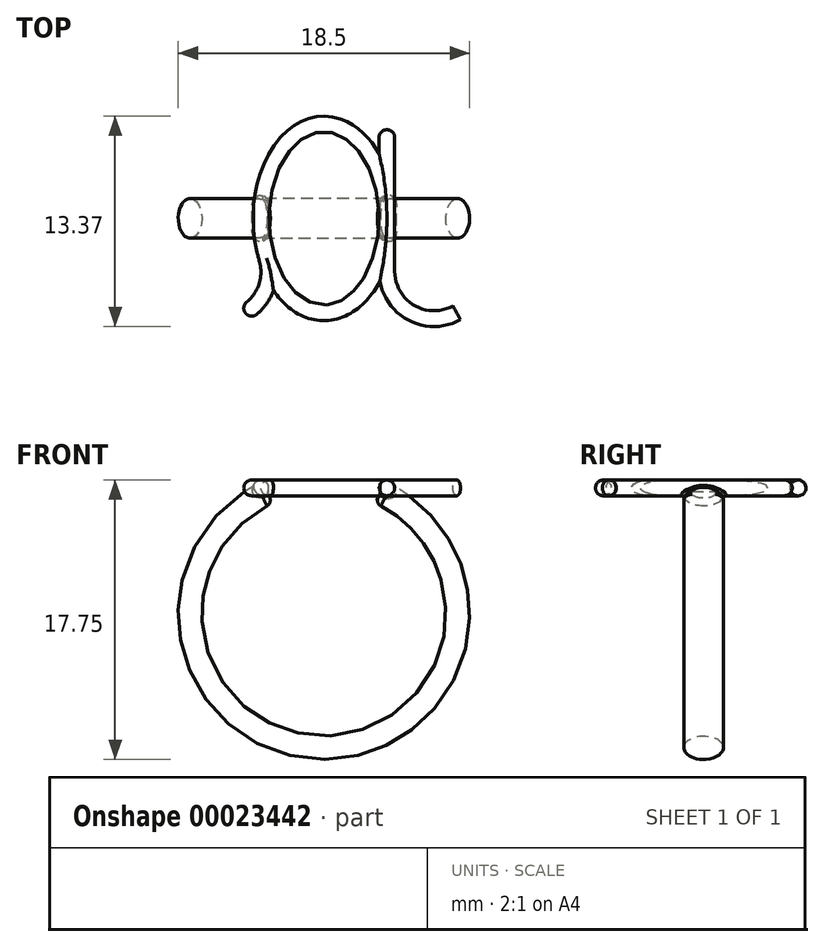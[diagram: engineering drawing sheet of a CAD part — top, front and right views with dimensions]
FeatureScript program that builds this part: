
annotation { "Feature Type Name" : "Feature", "Feature Type Description" : "" }
export const myFeature = defineFeature(function(context is Context, id is Id, definition is map)
    precondition{}
    {
        {
            var Q0;
            Q0=qCreatedBy(makeId("Right.planeOp"),FACE);
            var sketch = newSketch(context, id + "F0", { "sketchPlane" : qUnion([Q0])});
            skEllipse(sketch, "E0", {"center": v(0, -8.5) * mm, "majorRadius": 1.25 * mm, "minorRadius": 0.75 * mm, "majorAxis": v(1, 0)});
            skLineSegment(sketch, "E1", {"start": v(-8.37, 0) * mm, "end": v(10.93, 0) * mm, "construction": true});
            skSolve(sketch);
        }
        {
            var Q0;
            Q0=makeQuery(id+"F0.imprint","IMPRINT",FACE,{"disambiguationData":[TD([[makeQuery(id+"F0.imprint","IMPRINT",EDGE,{"derivedFrom":sQuery(id+"F0.wireOp",EDGE,"E0")}),1.0]])]});
            var Q1;
            Q1=sQuery(id+"F0.wireOp",EDGE,"E1");
            revolve(context, id + "F1", {"entities" : qUnion([Q0]), "axis" : qUnion([Q1]), "revolveType" : RevolveType.TWO_DIRECTIONS, "angle" : 155 * degree, "angleBack" : 205 * degree});
        }
        {
            var Q0;
            Q0=qCreatedBy(makeId("Top.planeOp"),FACE);
            cPlane(context, id + "F2", {"entities" : qUnion([Q0]), "cplaneType" : CPlaneType.OFFSET, "offset" : 8 * mm, "width" : 150 * mm, "height" : 150 * mm});
        }
        {
            var Q0;
            Q0=qCreatedBy(id+"F2.planeOp",FACE);
            var sketch = newSketch(context, id + "F3", { "sketchPlane" : qUnion([Q0])});
            skEllipse(sketch, "E2", {"center": v(0, 0) * mm, "majorRadius": 6 * mm, "minorRadius": 4 * mm, "majorAxis": v(0, 1)});
            skLineSegment(sketch, "E3", {"start": v(4, 5.63) * mm, "end": v(4, -3.37) * mm});
            skArc(sketch, "E4", {"start": v(4, -3.37) * mm, "mid": v(5.47, -5.95) * mm, "end": v(8.44, -6) * mm});
            skLineSegment(sketch, "E5", {"start": v(-7.83, -6) * mm, "end": v(11.12, -6) * mm, "construction": true});
            skArc(sketch, "E6", {"start": v(-5, -6) * mm, "mid": v(-3.7, -4.5) * mm, "end": v(-3.63, -2.52) * mm});
            skSolve(sketch);
        }
        {
            var Q0;
            Q0=sQuery(id+"F3.wireOp",VERTEX,"E3.start");
            var Q1;
            Q1=sQuery(id+"F3.wireOp",EDGE,"E3");
            cPlane(context, id + "F4", {"entities" : qUnion([Q0, Q1]), "cplaneType" : CPlaneType.LINE_POINT, "offset" : 150 * mm, "width" : 150 * mm, "height" : 150 * mm});
        }
        {
            var Q0;
            Q0=qCreatedBy(id+"F4.planeOp",FACE);
            var sketch = newSketch(context, id + "F5", { "sketchPlane" : qUnion([Q0])});
            skCircle(sketch, "E7", {"center": v(4, 8) * mm, "radius": 0.5 * mm});
            skSolve(sketch);
        }
        {
            var Q0;
            Q0=makeQuery(id+"F5.imprint","IMPRINT",FACE,{"disambiguationData":[TD([[makeQuery(id+"F5.imprint","IMPRINT",EDGE,{"derivedFrom":sQuery(id+"F5.wireOp",EDGE,"E7")}),1.0]])]});
            var Q1;
            Q1=sQuery(id+"F3.wireOp",EDGE,"E3");
            var Q2;
            Q2=sQuery(id+"F3.wireOp",EDGE,"E4");
            sweep(context, id + "F6", {"operationType" : NewBodyOperationType.ADD, "profiles" : qUnion([Q0]), "path" : qUnion([Q1, Q2])});
        }
        {
            var Q0;
            Q0=qCreatedBy(makeId("Right.planeOp"),FACE);
            var sketch = newSketch(context, id + "F7", { "sketchPlane" : qUnion([Q0])});
            skCircle(sketch, "E8", {"center": v(6, 8) * mm, "radius": 0.5 * mm});
            skLineSegment(sketch, "E9.0", {"start": v(-6, 8) * mm, "end": v(6, 8) * mm});
            skSolve(sketch);
        }
        {
            var Q0;
            Q0=makeQuery(id+"F7.imprint","IMPRINT",FACE,{"disambiguationData":[TD([[makeQuery(id+"F7.imprint","IMPRINT",EDGE,{"derivedFrom":sQuery(id+"F7.wireOp",EDGE,"E8")}),1.0]])]});
            var Q1;
            Q1=sQuery(id+"F3.wireOp",EDGE,"E2");
            sweep(context, id + "F8", {"operationType" : NewBodyOperationType.ADD, "profiles" : qUnion([Q0]), "path" : qUnion([Q1])});
        }
        {
            var Q0;
            Q0=sQuery(id+"F3.wireOp",VERTEX,"E6.start");
            var Q1;
            Q1=sQuery(id+"F3.wireOp",EDGE,"E6");
            cPlane(context, id + "F9", {"entities" : qUnion([Q0, Q1]), "cplaneType" : CPlaneType.CURVE_POINT, "offset" : 150 * mm, "width" : 150 * mm, "height" : 150 * mm});
        }
        {
            var Q0;
            Q0=qCreatedBy(id+"F9.planeOp",FACE);
            var sketch = newSketch(context, id + "F10", { "sketchPlane" : qUnion([Q0])});
            skCircle(sketch, "E10", {"center": v(-2.7, 8) * mm, "radius": 0.5 * mm});
            skSolve(sketch);
        }
        {
            var Q0;
            Q0=makeQuery(id+"F10.imprint","IMPRINT",FACE,{"disambiguationData":[TD([[makeQuery(id+"F10.imprint","IMPRINT",EDGE,{"derivedFrom":sQuery(id+"F10.wireOp",EDGE,"E10")}),1.0]])]});
            var Q1;
            Q1=sQuery(id+"F3.wireOp",EDGE,"E6");
            sweep(context, id + "F11", {"operationType" : NewBodyOperationType.ADD, "profiles" : qUnion([Q0]), "path" : qUnion([Q1])});
        }
        {
            var Q0;
            Q0=makeQuery(id+"F1.opRevolve","CAP_EDGE",EDGE,{"disambiguationData":[OSD([sQuery(id+"F0.wireOp",EDGE,"E0")])],"isStart":false});
            var Q1;
            Q1=makeQuery(id+"F1.opRevolve","CAP_EDGE",EDGE,{"disambiguationData":[OSD([sQuery(id+"F0.wireOp",EDGE,"E0")])],"isStart":true});
            fillet(context, id + "F12", {"entities" : qUnion([Q0, Q1]), "radius" : .4 * mm, "tangentPropagation" : true, "allowEdgeOverflow" : false});
        }
        {
            var Q0;
            Q0=makeQuery(id+"F6.opSweep","CAP_EDGE",EDGE,{"disambiguationData":[OSD([sQuery(id+"F3.wireOp",VERTEX,"E3.start"),sQuery(id+"F5.wireOp",EDGE,"E7")])],"isStart":true});
            var Q1;
            Q1=makeQuery(id+"F11.opSweep","CAP_EDGE",EDGE,{"disambiguationData":[OSD([sQuery(id+"F3.wireOp",VERTEX,"E6.start"),sQuery(id+"F10.wireOp",EDGE,"E10")])],"isStart":true});
            fillet(context, id + "F13", {"entities" : qUnion([Q0, Q1]), "radius" : .5 * mm, "tangentPropagation" : true, "allowEdgeOverflow" : false});
        }
        {
            var Q0;
            Q0=makeQuery(id+"F12.opFillet","BLEND_EDGE",EDGE,{"disambiguationData":[OD(0.0)],"blendedFrom":[makeQuery(id+"F1.opRevolve","CAP_EDGE",EDGE,{"disambiguationData":[OSD([sQuery(id+"F0.wireOp",EDGE,"E0")])],"isStart":true}),makeQuery(id+"F8.opSweep","SWEPT_FACE",FACE,{"disambiguationData":[OSD([sQuery(id+"F3.wireOp",EDGE,"E2"),sQuery(id+"F7.wireOp",EDGE,"E8")])]})],"blendedInto":[makeQuery(id+"F8.opSweep","SWEPT_FACE",FACE,{"disambiguationData":[OSD([sQuery(id+"F3.wireOp",EDGE,"E2"),sQuery(id+"F7.wireOp",EDGE,"E8")])]})]});
            var Q1;
            Q1=makeQuery(id+"F8.boolean.opBoolean","INTERSECT",EDGE,{"derivedFrom":[makeQuery(id+"F1.opRevolve","CAP_FACE",FACE,{"disambiguationData":[OSD([sQuery(id+"F0.wireOp",EDGE,"E0")])],"isStart":true}),makeQuery(id+"F8.opSweep","SWEPT_FACE",FACE,{"disambiguationData":[OSD([sQuery(id+"F3.wireOp",EDGE,"E2"),sQuery(id+"F7.wireOp",EDGE,"E8")])]})]});
            var Q2;
            Q2=makeQuery(id+"F6.boolean.opBoolean","INTERSECT",EDGE,{"derivedFrom":[makeQuery(id+"F1.opRevolve","SWEPT_FACE",FACE,{"disambiguationData":[OSD([sQuery(id+"F0.wireOp",EDGE,"E0")])]}),makeQuery(id+"F6.opSweep","SWEPT_FACE",FACE,{"disambiguationData":[OSD([sQuery(id+"F3.wireOp",EDGE,"E3"),sQuery(id+"F5.wireOp",EDGE,"E7")])]})]});
            var Q3;
            Q3=makeQuery(id+"F12.opFillet","BLEND_EDGE",EDGE,{"disambiguationData":[OD(1.0)],"blendedFrom":[makeQuery(id+"F1.opRevolve","CAP_EDGE",EDGE,{"disambiguationData":[OSD([sQuery(id+"F0.wireOp",EDGE,"E0")])],"isStart":true}),makeQuery(id+"F8.opSweep","SWEPT_FACE",FACE,{"disambiguationData":[OSD([sQuery(id+"F3.wireOp",EDGE,"E2"),sQuery(id+"F7.wireOp",EDGE,"E8")])]})],"blendedInto":[makeQuery(id+"F8.opSweep","SWEPT_FACE",FACE,{"disambiguationData":[OSD([sQuery(id+"F3.wireOp",EDGE,"E2"),sQuery(id+"F7.wireOp",EDGE,"E8")])]})]});
            var Q4;
            Q4=makeQuery(id+"F12.opFillet","BLEND_EDGE",EDGE,{"disambiguationData":[OD(1.0)],"blendedFrom":[makeQuery(id+"F1.opRevolve","CAP_EDGE",EDGE,{"disambiguationData":[OSD([sQuery(id+"F0.wireOp",EDGE,"E0")])],"isStart":false}),makeQuery(id+"F8.opSweep","SWEPT_FACE",FACE,{"disambiguationData":[OSD([sQuery(id+"F3.wireOp",EDGE,"E2"),sQuery(id+"F7.wireOp",EDGE,"E8")])]})],"blendedInto":[makeQuery(id+"F8.opSweep","SWEPT_FACE",FACE,{"disambiguationData":[OSD([sQuery(id+"F3.wireOp",EDGE,"E2"),sQuery(id+"F7.wireOp",EDGE,"E8")])]})]});
            var Q5;
            {var subQ0=sQuery(id+"F0.wireOp",EDGE,"E0");Q5=makeQuery(id+"F12.opFillet","BLEND_EDGE",EDGE,{"blendedFrom":[makeQuery(id+"F1.opRevolve","CAP_EDGE",EDGE,{"disambiguationData":[OSD([subQ0])],"isStart":false}),makeQuery(id+"F1.opRevolve","CAP_FACE",FACE,{"disambiguationData":[OSD([subQ0])],"isStart":false})],"blendedInto":[makeQuery(id+"F1.opRevolve","CAP_FACE",FACE,{"disambiguationData":[OSD([subQ0])],"isStart":false})]});}
            var Q6;
            Q6=makeQuery(id+"F8.boolean.opBoolean","INTERSECT",EDGE,{"disambiguationData":[OD(2.0)],"derivedFrom":[makeQuery(id+"F1.opRevolve","SWEPT_FACE",FACE,{"disambiguationData":[OSD([sQuery(id+"F0.wireOp",EDGE,"E0")])]}),makeQuery(id+"F8.opSweep","SWEPT_FACE",FACE,{"disambiguationData":[OSD([sQuery(id+"F3.wireOp",EDGE,"E2"),sQuery(id+"F7.wireOp",EDGE,"E8")])]})]});
            var Q7;
            Q7=makeQuery(id+"F12.opFillet","BLEND_EDGE",EDGE,{"disambiguationData":[OD(0.0)],"blendedFrom":[makeQuery(id+"F1.opRevolve","CAP_EDGE",EDGE,{"disambiguationData":[OSD([sQuery(id+"F0.wireOp",EDGE,"E0")])],"isStart":false}),makeQuery(id+"F8.opSweep","SWEPT_FACE",FACE,{"disambiguationData":[OSD([sQuery(id+"F3.wireOp",EDGE,"E2"),sQuery(id+"F7.wireOp",EDGE,"E8")])]})],"blendedInto":[makeQuery(id+"F8.opSweep","SWEPT_FACE",FACE,{"disambiguationData":[OSD([sQuery(id+"F3.wireOp",EDGE,"E2"),sQuery(id+"F7.wireOp",EDGE,"E8")])]})]});
            fillet(context, id + "F14", {"entities" : qUnion([Q0, Q1, Q2, Q3, Q4, Q5, Q6, Q7]), "radius" : .2 * mm, "tangentPropagation" : true, "allowEdgeOverflow" : false});
        }
        {
            var Q0;
            Q0=makeQuery(id+"F6.opSweep","CAP_FACE",FACE,{"disambiguationData":[OSD([sQuery(id+"F3.wireOp",VERTEX,"E4.end"),sQuery(id+"F5.wireOp",EDGE,"E7")])],"isStart":false});
            cPlane(context, id + "F15", {"entities" : qUnion([Q0]), "cplaneType" : CPlaneType.OFFSET, "offset" : 0 * mm, "width" : 150 * mm, "height" : 150 * mm});
        }
        {
            var Q0;
            Q0=qCreatedBy(id+"F15.planeOp",FACE);
            cPlane(context, id + "F16", {"entities" : qUnion([Q0]), "cplaneType" : CPlaneType.OFFSET, "offset" : 1.5 * mm, "width" : 150 * mm, "height" : 150 * mm});
        }
        {
            var Q0;
            Q0=qCreatedBy(id+"F16.planeOp",FACE);
            cPlane(context, id + "F17", {"entities" : qUnion([Q0]), "cplaneType" : CPlaneType.OFFSET, "offset" : 2.5 * mm, "width" : 150 * mm, "height" : 150 * mm});
        }
        {
            var Q0;
            Q0=qCreatedBy(id+"F15.planeOp",FACE);
            var sketch = newSketch(context, id + "F18", { "sketchPlane" : qUnion([Q0])});
            skPoint(sketch, "E11", {"position": v(-9.32, 8) * mm});
            skCircle(sketch, "E12.0.0", {"center": v(-9.32, 8) * mm, "radius": 0.5 * mm});
            skSolve(sketch);
        }
        {
            var Q0;
            Q0=qCreatedBy(id+"F16.planeOp",FACE);
            var sketch = newSketch(context, id + "F19", { "sketchPlane" : qUnion([Q0])});
            skLineSegment(sketch, "E13", {"start": v(-7.32, 9.11) * mm, "end": v(-7.32, 6.5) * mm, "construction": true});
            skLineSegment(sketch, "E14", {"start": v(-11.32, 9.41) * mm, "end": v(-11.32, 7.2) * mm, "construction": true});
            skEllipticalArc(sketch, "E15", {});
            skEllipticalArc(sketch, "E16", {});
            skLineSegment(sketch, "E17", {"start": v(-11.32, 8) * mm, "end": v(-7.32, 8) * mm});
            const initialGuessF19  = {"E15": [-0.009315497004728895, 0.008, 1, 0, 0.002, 0.00065, 3.141592653589793, 0], "E16": [-0.009315497004728895, 0.008, 1, 0, 0.002, 0.00065, 0, 3.141592653589793]};
            skSetInitialGuess(sketch, initialGuessF19);
            skSolve(sketch);
        }
        {
            var Q0;
            Q0=qCreatedBy(id+"F17.planeOp",FACE);
            var sketch = newSketch(context, id + "F20", { "sketchPlane" : qUnion([Q0])});
            skPoint(sketch, "E18", {"position": v(-9.32, 8) * mm});
            skSolve(sketch);
        }
        {
            var Q0;
            Q0=qCreatedBy(id+"F2.planeOp",FACE);
            var sketch = newSketch(context, id + "F21", { "sketchPlane" : qUnion([Q0])});
            skArc(sketch, "E19", {"start": v(8.8, -3.53) * mm, "mid": v(7.68, -4.63) * mm, "end": v(8.44, -6) * mm});
            skArc(sketch, "E20", {"start": v(8.8, -3.53) * mm, "mid": v(10.23, -3.53) * mm, "end": v(11.6, -3.92) * mm});
            skPoint(sketch, "E21", {"position": v(8.8, -3.53) * mm});
            skArc(sketch, "E22.0", {"start": v(4, -3.37) * mm, "mid": v(5.47, -5.95) * mm, "end": v(8.44, -6) * mm});
            skLineSegment(sketch, "E23", {"start": v(8.44, -6) * mm, "end": v(11.95, -4.08) * mm});
            skArc(sketch, "E24.MirrorCS", {"start": v(10.72, -7.03) * mm, "mid": v(11.49, -5.83) * mm, "end": v(11.9, -4.45) * mm});
            skArc(sketch, "E25.MirrorCS", {"start": v(10.72, -7.03) * mm, "mid": v(9.19, -7.38) * mm, "end": v(8.44, -6) * mm});
            skPoint(sketch, "E26.visualSharp", {"position": v(11.95, -4.08) * mm});
            skArc(sketch, "E26.filletArc", {"start": v(11.9, -4.45) * mm, "mid": v(11.85, -4.13) * mm, "end": v(11.6, -3.92) * mm});
            skSolve(sketch);
        }
        {
            var Q0;
            Q0=sQuery(id+"F21.wireOp",EDGE,"E23");
            cPlane(context, id + "F22", {"entities" : qUnion([Q0]), "cplaneType" : CPlaneType.LINE_ANGLE, "offset" : 150 * mm, "angle" : 0 * degree, "width" : 150 * mm, "height" : 150 * mm});
        }
    });
